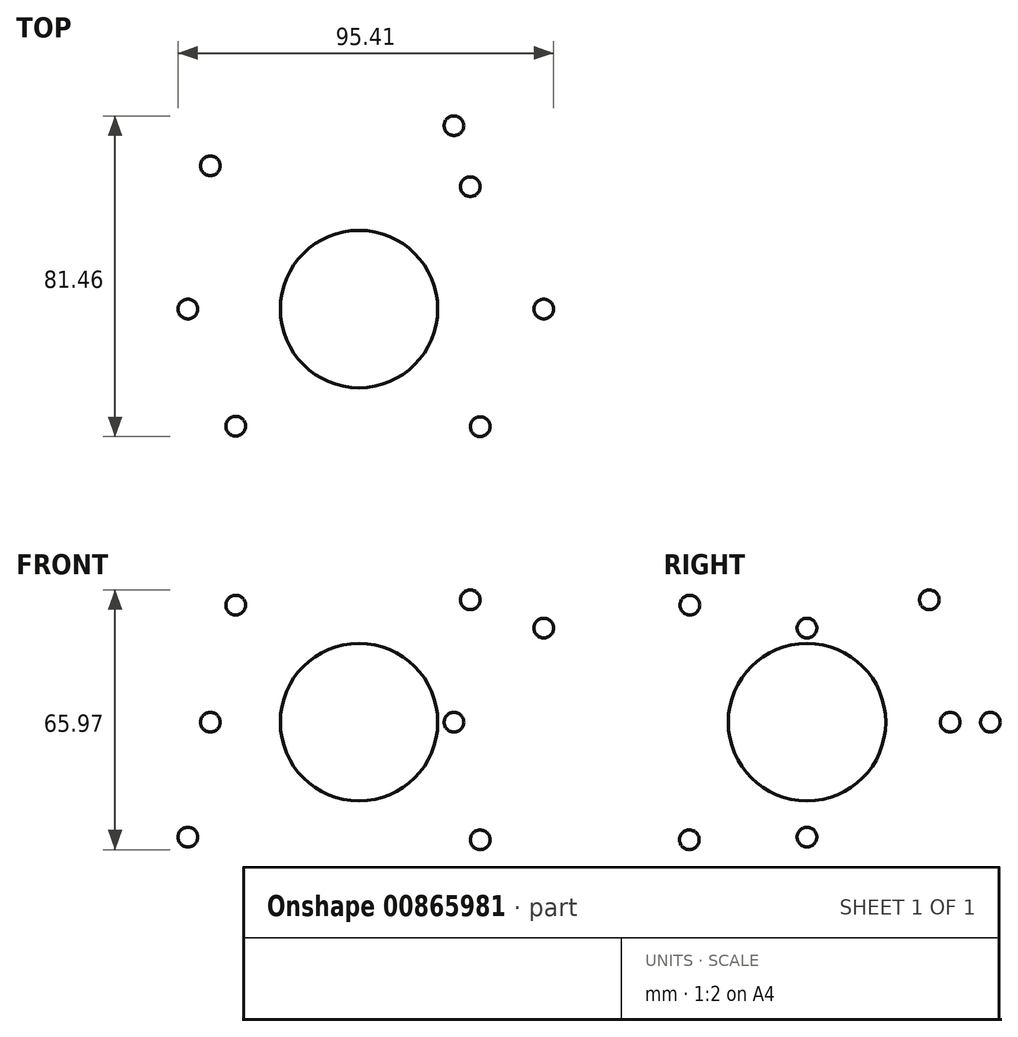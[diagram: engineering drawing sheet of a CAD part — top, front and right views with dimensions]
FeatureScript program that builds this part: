
annotation { "Feature Type Name" : "Feature", "Feature Type Description" : "" }
export const myFeature = defineFeature(function(context is Context, id is Id, definition is map)
    precondition{}
    {
        {
            var Q0;
            Q0=qCreatedBy(makeId("Front.planeOp"),FACE);
            var sketch = newSketch(context, id + "F0", { "sketchPlane" : qUnion([Q0])});
            skLineSegment(sketch, "E0", {"start": v(-75, 0) * mm, "end": v(76.66, 0) * mm});
            skSolve(sketch);
        }
        {
            var Q0;
            Q0=sQuery(id+"F0.wireOp",EDGE,"E0");
            cPlane(context, id + "F1", {"entities" : qUnion([Q0]), "cplaneType" : CPlaneType.LINE_ANGLE, "offset" : 25 * mm, "angle" : 45 * degree, "width" : 150 * mm, "height" : 150 * mm});
        }
        {
            var Q0;
            Q0=sQuery(id+"F0.wireOp",EDGE,"E0");
            cPlane(context, id + "F2", {"entities" : qUnion([Q0]), "cplaneType" : CPlaneType.LINE_ANGLE, "offset" : 25 * mm, "angle" : 135 * degree, "width" : 150 * mm, "height" : 150 * mm});
        }
        {
            var Q0;
            Q0=qCreatedBy(makeId("Right.planeOp"),FACE);
            var sketch = newSketch(context, id + "F3", { "sketchPlane" : qUnion([Q0])});
            skLineSegment(sketch, "E1", {"start": v(74.68, 0) * mm, "end": v(-74.48, 0) * mm});
            skSolve(sketch);
        }
        {
            var Q0;
            Q0=qCreatedBy(makeId("Top.planeOp"),FACE);
            var sketch = newSketch(context, id + "F4", { "sketchPlane" : qUnion([Q0])});
            skLineSegment(sketch, "E2", {"start": v(0, -20) * mm, "end": v(0, 20) * mm});
            skArc(sketch, "E3", {"start": v(0, 20) * mm, "mid": v(-20, 0) * mm, "end": v(0, -20) * mm});
            skSolve(sketch);
        }
        {
            var Q0;
            Q0 = qSketchRegion(id + "F4", true);
            var Q1;
            Q1=sQuery(id+"F4.wireOp",EDGE,"E2");
            revolve(context, id + "F5", {"surfaceOperationType" : NewSurfaceOperationType.NEW, "entities" : qUnion([Q0]), "axis" : qUnion([Q1]), "revolveType" : RevolveType.FULL});
        }
        {
            var Q0;
            Q0=qCreatedBy(makeId("Top.planeOp"),FACE);
            var sketch = newSketch(context, id + "F6", { "sketchPlane" : qUnion([Q0])});
            skLineSegment(sketch, "E4", {"start": v(24.11, 46.58) * mm, "end": v(24.11, 44.08) * mm});
            skLineSegment(sketch, "E5", {"start": v(24.11, 44.08) * mm, "end": v(24.11, 49.08) * mm});
            skArc(sketch, "E6", {"start": v(24.11, 49.08) * mm, "mid": v(21.61, 46.58) * mm, "end": v(24.11, 44.08) * mm});
            skSolve(sketch);
        }
        {
            var Q0;
            Q0 = qSketchRegion(id + "F6", true);
            var Q1;
            Q1=sQuery(id+"F6.wireOp",EDGE,"E5");
            revolve(context, id + "F7", {"surfaceOperationType" : NewSurfaceOperationType.NEW, "entities" : qUnion([Q0]), "axis" : qUnion([Q1]), "revolveType" : RevolveType.FULL});
        }
        {
            var Q0;
            Q0=qCreatedBy(id+"F1.planeOp",FACE);
            var sketch = newSketch(context, id + "F8", { "sketchPlane" : qUnion([Q0])});
            skLineSegment(sketch, "E7", {"start": v(31.33, 39.57) * mm, "end": v(31.33, 44.57) * mm});
            skArc(sketch, "E8", {"start": v(31.33, 44.57) * mm, "mid": v(28.83, 42.07) * mm, "end": v(31.33, 39.57) * mm});
            skSolve(sketch);
        }
        {
            var Q0;
            Q0 = qSketchRegion(id + "F8", true);
            var Q1;
            Q1=sQuery(id+"F8.wireOp",EDGE,"E7");
            revolve(context, id + "F9", {"surfaceOperationType" : NewSurfaceOperationType.NEW, "entities" : qUnion([Q0]), "axis" : qUnion([Q1]), "revolveType" : RevolveType.FULL});
        }
        {
            var Q0;
            Q0=qCreatedBy(id+"F2.planeOp",FACE);
            var sketch = newSketch(context, id + "F10", { "sketchPlane" : qUnion([Q0])});
            skLineSegment(sketch, "E9", {"start": v(28.26, 43.96) * mm, "end": v(28.26, 41.46) * mm});
            skLineSegment(sketch, "E10", {"start": v(28.26, 41.46) * mm, "end": v(28.26, 46.46) * mm});
            skLineSegment(sketch, "E11", {"start": v(28.26, 46.46) * mm, "end": v(28.26, 46.46) * mm});
            skArc(sketch, "E12", {"start": v(27.91, 41.49) * mm, "mid": v(30.76, 43.79) * mm, "end": v(28.26, 46.46) * mm});
            skSolve(sketch);
        }
        {
            var Q0;
            Q0 = qSketchRegion(id + "F10", true);
            var Q1;
            Q1=sQuery(id+"F10.wireOp",EDGE,"E10");
            revolve(context, id + "F11", {"surfaceOperationType" : NewSurfaceOperationType.NEW, "entities" : qUnion([Q0]), "axis" : qUnion([Q1]), "revolveType" : RevolveType.FULL});
        }
        {
            var Q0;
            Q0=qCreatedBy(makeId("Front.planeOp"),FACE);
            var sketch = newSketch(context, id + "F12", { "sketchPlane" : qUnion([Q0])});
            skLineSegment(sketch, "E13", {"start": v(-43.48, -31.69) * mm, "end": v(-43.48, -26.69) * mm});
            skArc(sketch, "E14", {"start": v(-43.48, -26.69) * mm, "mid": v(-45.98, -29.19) * mm, "end": v(-43.48, -31.69) * mm});
            skSolve(sketch);
        }
        {
            var Q0;
            Q0 = qSketchRegion(id + "F12", true);
            var Q1;
            Q1=sQuery(id+"F12.wireOp",EDGE,"E13");
            revolve(context, id + "F13", {"surfaceOperationType" : NewSurfaceOperationType.NEW, "entities" : qUnion([Q0]), "axis" : qUnion([Q1]), "revolveType" : RevolveType.FULL});
        }
        {
            var Q0;
            Q0=qCreatedBy(makeId("Top.planeOp"),FACE);
            var sketch = newSketch(context, id + "F14", { "sketchPlane" : qUnion([Q0])});
            skLineSegment(sketch, "E15", {"start": v(-37.77, 33.89) * mm, "end": v(-37.77, 38.89) * mm});
            skArc(sketch, "E16", {"start": v(-37.77, 38.89) * mm, "mid": v(-40.27, 36.39) * mm, "end": v(-37.77, 33.89) * mm});
            skSolve(sketch);
        }
        {
            var Q0;
            Q0 = qSketchRegion(id + "F14", true);
            var Q1;
            Q1=sQuery(id+"F14.wireOp",EDGE,"E15");
            revolve(context, id + "F15", {"surfaceOperationType" : NewSurfaceOperationType.NEW, "entities" : qUnion([Q0]), "axis" : qUnion([Q1]), "revolveType" : RevolveType.FULL});
        }
        {
            var Q0;
            Q0=qCreatedBy(id+"F2.planeOp",FACE);
            var sketch = newSketch(context, id + "F16", { "sketchPlane" : qUnion([Q0])});
            skCircle(sketch, "E17", {"center": v(30.78, -42.26) * mm, "radius": 2.5 * mm});
            skLineSegment(sketch, "E18", {"start": v(30.78, -44.76) * mm, "end": v(30.78, -39.76) * mm});
            skSolve(sketch);
        }
        {
            var Q0;
            {var subQ0=sQuery(id+"F16.wireOp",EDGE,"E18");Q0=makeQuery(id+"F16.imprint","IMPRINT",FACE,{"disambiguationData":[TD([[makeQuery(id+"F16.imprint","IMPRINT",EDGE,{"derivedFrom":subQ0}),-1.0]])]});}
            var Q1;
            Q1=sQuery(id+"F16.wireOp",EDGE,"E18");
            revolve(context, id + "F17", {"surfaceOperationType" : NewSurfaceOperationType.NEW, "entities" : qUnion([Q0]), "axis" : qUnion([Q1]), "revolveType" : RevolveType.FULL});
        }
        {
            var Q0;
            Q0=qCreatedBy(makeId("Front.planeOp"),FACE);
            var sketch = newSketch(context, id + "F18", { "sketchPlane" : qUnion([Q0])});
            skLineSegment(sketch, "E19", {"start": v(46.93, 21.4) * mm, "end": v(46.93, 26.4) * mm});
            skLineSegment(sketch, "E20", {"start": v(46.93, 26.4) * mm, "end": v(46.93, 26.4) * mm});
            skArc(sketch, "E21", {"start": v(46.93, 26.4) * mm, "mid": v(44.43, 23.9) * mm, "end": v(46.93, 21.4) * mm});
            skSolve(sketch);
        }
        {
            var Q0;
            Q0 = qSketchRegion(id + "F18", true);
            var Q1;
            Q1=sQuery(id+"F18.wireOp",EDGE,"E19");
            revolve(context, id + "F19", {"surfaceOperationType" : NewSurfaceOperationType.NEW, "entities" : qUnion([Q0]), "axis" : qUnion([Q1]), "revolveType" : RevolveType.FULL});
        }
    });
